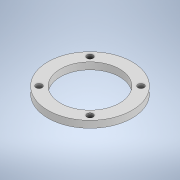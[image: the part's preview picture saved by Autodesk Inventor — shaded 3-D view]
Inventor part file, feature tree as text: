
AUTODESK INVENTOR PART (.ipt)
format: ipt  version: 2021 (Build 250183000, 183)  size: 117,760 bytes
history: native  units: mm
features: sketch x2, extrude x1, hole x1
ambient origin geometry x8: Origin, YZ Plane, XZ Plane, XY Plane, X Axis, Y Axis, Z Axis, Center Point
bodies: Solid1 (feature_tree)
feature tree (4):
  extrude  "Extrusion1"  Depth=61.0mm
  hole  "Hole1"  [1 undecoded]
  sketch  "Sketch1"  dims[d0=43.0mm d1=61.0mm]
  sketch  "Sketch2"  dims[d2=5.0mm d3=0.0mm d4=37.0mm d5=37.0mm d6=4.496mm d7=5.0mm d8=8.433mm d9=2.0mm d10=14.3117mm d11=6.0mm d12=0.0mm]
note: 1 required parameter value undecoded (feature->parameter linkage not recoverable at this tier; creation-order binding heuristic only, values carry confidence <= 0.55)
